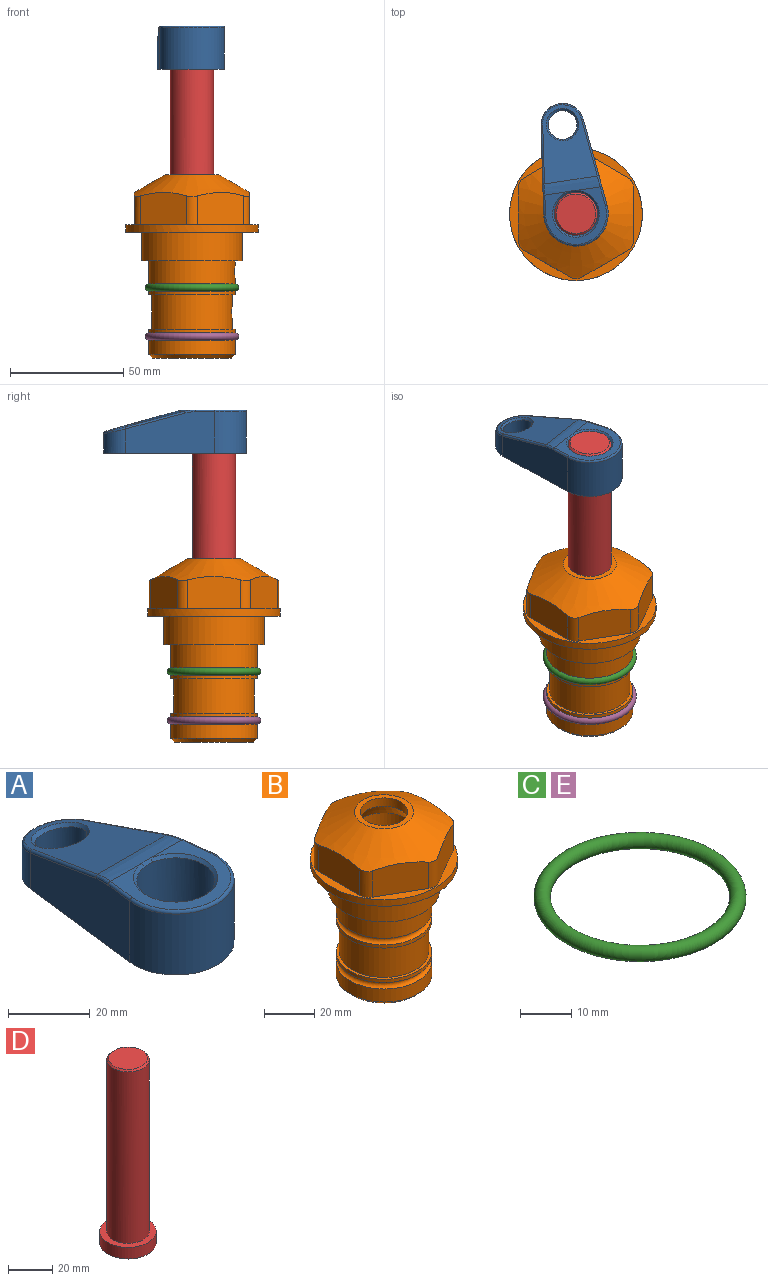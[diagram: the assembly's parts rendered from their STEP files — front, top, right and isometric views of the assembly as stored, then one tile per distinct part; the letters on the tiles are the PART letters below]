
ASSEMBLY  parts=5 mates=4
PART A: 31 faces, bbox 31.7x65.5x19.8 mm
  f0: plane 39.12x18.26mm, normal (0.99,0.12,0), area 612.2mm2, adj f1,f4,f7,f11,f13,f15
  f1: cylinder r=9.53mm len=18.91mm, axis (0,0,-1), area 296.1mm2, adj f0,f2,f7,f17
  f2: plane 39.12x18.26mm, normal (-0.99,0.12,0), area 612.2mm2, adj f1,f4,f7,f12,f14,f16
  f3: cylinder r=6.35mm len=12.7mm, axis (0,0,-1), area 362.4mm2, adj f7,f18
  f4: cylinder r=14.29mm len=28.58mm, axis (0,0,-1), area 882.2mm2, adj f0,f2,f7,f10
  f5: cylinder r=9.53mm len=19.05mm, axis (0,0,-1), area 1092.6mm2, adj f7,f19,f20
  f6: plane 26.99x23.69mm, normal (0,0,1), area 216.2mm2, adj f9,f10,f11,f12,f19
  f7: plane 63.5x28.58mm, normal (0,0,-1), area 661.8mm2, adj f0,f1,f2,f3,f4,f5,f22,f23
  f8: plane 33.52x23.6mm, normal (0,0.26,0.97), area 486mm2, adj f9,f15,f16,f17,f18
  f9: cylinder r=19.05mm len=24.72mm, axis (1,0,0), area 120.4mm2, adj f6,f8,f13,f14,f20
  f10: torus R=13.49mm, axis (0,0,1), area 59mm2, adj f4,f6,f11,f12
  f11: cylinder r=0.79mm len=8.67mm, axis (0.12,-0.99,0), area 10.8mm2, adj f0,f6,f10,f13
  f12: cylinder r=0.79mm len=8.67mm, axis (0.12,0.99,0), area 10.8mm2, adj f2,f6,f10,f14
  f13: bspline ~4.95x1.42mm, area 6.1mm2, adj f0,f9,f11,f15
  f14: bspline ~4.95x1.42mm, area 6.1mm2, adj f2,f9,f12,f16
  f15: cylinder r=0.79mm len=25.95mm, axis (0.12,-0.96,0.26), area 32.9mm2, adj f0,f8,f13,f17
  f16: cylinder r=0.79mm len=25.95mm, axis (0.12,0.96,-0.26), area 32.9mm2, adj f2,f8,f14,f17
  f17: bspline ~18.91x8.38mm, area 30mm2, adj f1,f8,f15,f16
  f18: bspline ~14.29x14.29mm, area 48.3mm2, adj f3,f8
  f19: cone r=9.53mm half-angle=45deg, axis (0,0,1), area 66.5mm2, adj f5,f6,f20
  f20: bspline ~3.22x0.96mm, area 3.5mm2, adj f5,f9,f19
  f21: plane 2.75x2.72mm, normal (0,0,-1), area 2.9mm2, adj f23,f25,f28
  f22: plane 23.05x15.88mm, normal (-0.99,-0.12,0), area 323.6mm2, adj f7,f25,f26,f27,f28,f29
  f23: plane 23.05x15.88mm, normal (0.99,-0.12,0), area 323.6mm2, adj f7,f21,f25,f27,f28,f30
  f24: cylinder r=9.53mm len=10.69mm, axis (0,0,-1), area 114.7mm2, adj f7,f27,f29,f30
  f25: cylinder r=12.7mm len=20.59mm, axis (0,0,-1), area 381.1mm2, adj f7,f21,f22,f23,f26,f28
  f26: plane 2.75x2.72mm, normal (0,0,-1), area 2.9mm2, adj f22,f25,f28
  f27: plane 19.72x18.37mm, normal (0,-0.26,-0.97), area 291.8mm2, adj f22,f23,f24,f28,f29,f30
  f28: cylinder r=15.88mm len=19.92mm, axis (1,0,0), area 54.8mm2, adj f21,f22,f23,f25,f26,f27
  f29: cylinder r=1.59mm len=11mm, axis (0,0,-1), area 34.7mm2, adj f7,f22,f24,f27
  f30: cylinder r=1.59mm len=11mm, axis (0,0,-1), area 34.7mm2, adj f7,f23,f24,f27
PART B: 36 faces, bbox 58.7x58.7x81 mm
  f0: cylinder r=17.78mm len=35.56mm, axis (0,0,1), area 1670.8mm2, adj f23,f24,f31
  f1: cylinder r=19.05mm len=38.1mm, axis (0,0,1), area 1191.9mm2, adj f26,f27,f30
  f2: plane 58.66x58.66mm, normal (0,0,-1), area 1150.6mm2, adj f3,f28
  f3: cylinder r=29.33mm len=58.66mm, axis (0,0,-1), area 585.1mm2, adj f2,f4
  f4: plane 58.66x58.66mm, normal (0,0,1), area 475.9mm2, adj f3,f5,f6,f7,f8,f9,f10,f11
  f5: plane 20.32x14.34mm, normal (-0.5,0.87,0), area 324.4mm2, adj f4,f15,f16,f17
  f6: plane 20.32x14.34mm, normal (0.5,0.87,0), area 324.4mm2, adj f4,f14,f15,f17
  f7: plane 23.48x14.34mm, normal (1,0,0), area 324.4mm2, adj f4,f13,f14,f17
  f8: plane 20.32x14.34mm, normal (0.5,-0.87,0), area 324.4mm2, adj f4,f12,f13,f17
  f9: plane 20.32x14.34mm, normal (-0.5,-0.87,0), area 324.4mm2, adj f4,f11,f12,f17
  f10: plane 23.48x14.34mm, normal (-1,0,0), area 324.4mm2, adj f4,f11,f16,f17
  f11: cylinder r=5.08mm len=12.85mm, axis (0,0,-1), area 67.2mm2, adj f4,f9,f10,f17
  f12: cylinder r=5.08mm len=12.85mm, axis (0,0,-1), area 67.2mm2, adj f4,f8,f9,f17
  f13: cylinder r=5.08mm len=12.85mm, axis (0,0,-1), area 67.2mm2, adj f4,f7,f8,f17
  f14: cylinder r=5.08mm len=12.85mm, axis (0,0,-1), area 67.2mm2, adj f4,f6,f7,f17
  f15: cylinder r=5.08mm len=12.85mm, axis (0,0,-1), area 67.2mm2, adj f4,f5,f6,f17
  f16: cylinder r=5.08mm len=12.85mm, axis (0,0,-1), area 67.2mm2, adj f4,f5,f10,f17
  f17: cone r=11.73mm half-angle=60deg, axis (0,0,-1), area 2071.8mm2, adj f5,f6,f7,f8,f9,f10,f11,f12
  f18: plane 23.46x23.46mm, normal (0,0,1), area 147.4mm2, adj f17,f35
  f19: plane 34.93x34.93mm, normal (0,0,-1), area 958mm2, adj f29
  f20: cylinder r=19.05mm len=38.1mm, axis (0,0,1), area 760.1mm2, adj f21,f29
  f21: torus R=19.05mm, axis (0,0,1), area 565.3mm2, adj f20,f22
  f22: cylinder r=19.05mm len=38.1mm, axis (0,0,1), area 190mm2, adj f21,f23
  f23: plane 38.1x38.1mm, normal (0,0,1), area 146.9mm2, adj f0,f22
  f24: plane 38.1x38.1mm, normal (0,0,-1), area 146.9mm2, adj f0,f25
  f25: cylinder r=19.05mm len=38.1mm, axis (0,0,1), area 190mm2, adj f24,f26
  f26: torus R=19.05mm, axis (0,0,1), area 565.3mm2, adj f1,f25
  f27: plane 44.45x44.45mm, normal (0,0,-1), area 411.7mm2, adj f1,f28
  f28: cylinder r=22.23mm len=44.45mm, axis (0,0,1), area 1773.5mm2, adj f2,f27
  f29: cone r=19.05mm half-angle=45deg, axis (0,0,1), area 257.5mm2, adj f19,f20
  f30: cylinder r=3.17mm len=6.75mm, axis (-1,0,0), area 128mm2, adj f1,f33
  f31: cylinder r=3.17mm len=6.35mm, axis (-1,0,0), area 102.5mm2, adj f0,f33
  f32: plane 25.4x25.4mm, normal (0,0,1), area 506.7mm2, adj f33
  f33: cylinder r=12.7mm len=66.42mm, axis (0,0,-1), area 5236.2mm2, adj f30,f31,f32,f34
  f34: cone r=9.53mm half-angle=30deg, axis (0,0,-1), area 443.4mm2, adj f33,f35
  f35: cylinder r=9.53mm len=19.05mm, axis (0,0,-1), area 240.9mm2, adj f18,f34
PART C: 1 faces, bbox 44.7x44.7x3.2 mm
  f0: torus R=19.05mm, axis (0,0,1), area 1193.9mm2
PART D: 6 faces, bbox 25.4x25.4x101.6 mm
  f0: plane 17.46x17.46mm, normal (0,0,1), area 239.5mm2, adj f5
  f1: plane 25.4x25.4mm, normal (0,0,-1), area 506.7mm2, adj f2
  f2: cylinder r=12.7mm len=25.4mm, axis (0,0,1), area 506.7mm2, adj f1,f3
  f3: plane 25.4x25.4mm, normal (0,0,1), area 221.7mm2, adj f2,f4
  f4: cylinder r=9.53mm len=94.46mm, axis (0,0,1), area 5653mm2, adj f3,f5
  f5: cone r=8.73mm half-angle=45deg, axis (0,0,-1), area 64.4mm2, adj f0,f4
PART E: same geometry as C
PLACE A rot(axis=(0,0,1),8.6deg) t=(0,0,27.55)mm
PLACE B at identity fixed
PLACE C at identity
PLACE D rot(axis=(0,0,1),8.6deg) t=(0,0,27.55)mm
PLACE E t=(0,0,-21.59)mm
MATE fastened E.f0 <-> B.f0  axis (0,0,1) through (0,0,-46.1)mm
MATE fastened D.f2 <-> A.f4  axis (0,0,1) through (0,0,91.05)mm
MATE fastened C.f0 <-> B.f0  axis (0,0,1) through (0,0,-24.51)mm
MATE cylindrical B.f0 <-> D.f2  axis (0,0,1) through (0,0,-50.55)mm
